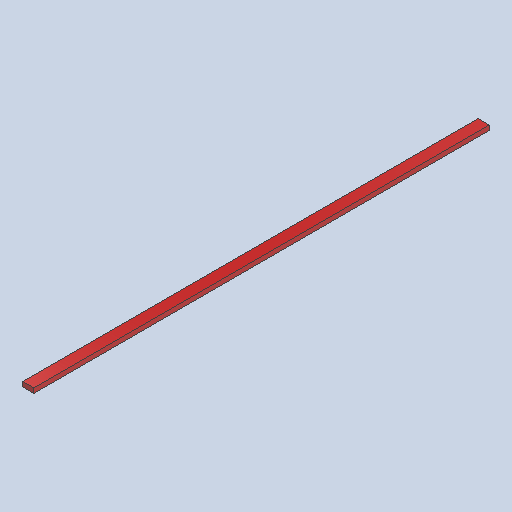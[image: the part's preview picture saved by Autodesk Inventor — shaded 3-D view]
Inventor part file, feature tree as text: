
AUTODESK INVENTOR PART (.ipt)
format: ipt  version: 2025.1 (Build 291241020, 241B)  size: 139,264 bytes
history: native  units: in
note: dims shown in document units (in); Inventor stores cm internally (conversion verified against a paired STEP export)
features: extrude x1, sketch x1, other x1
ambient origin geometry x8: Origin, YZ Plane, XZ Plane, XY Plane, X Axis, Y Axis, Z Axis, Center Point
bodies: Solid1 (feature_tree)
feature tree (3):
  extrude  "Extrusion1"  Depth=1.5in
  sketch  "Sketch1"  dims[d0=3.5in d1=1.5in d2=144.0in d3=0.0in]
  other  "Finish1"
